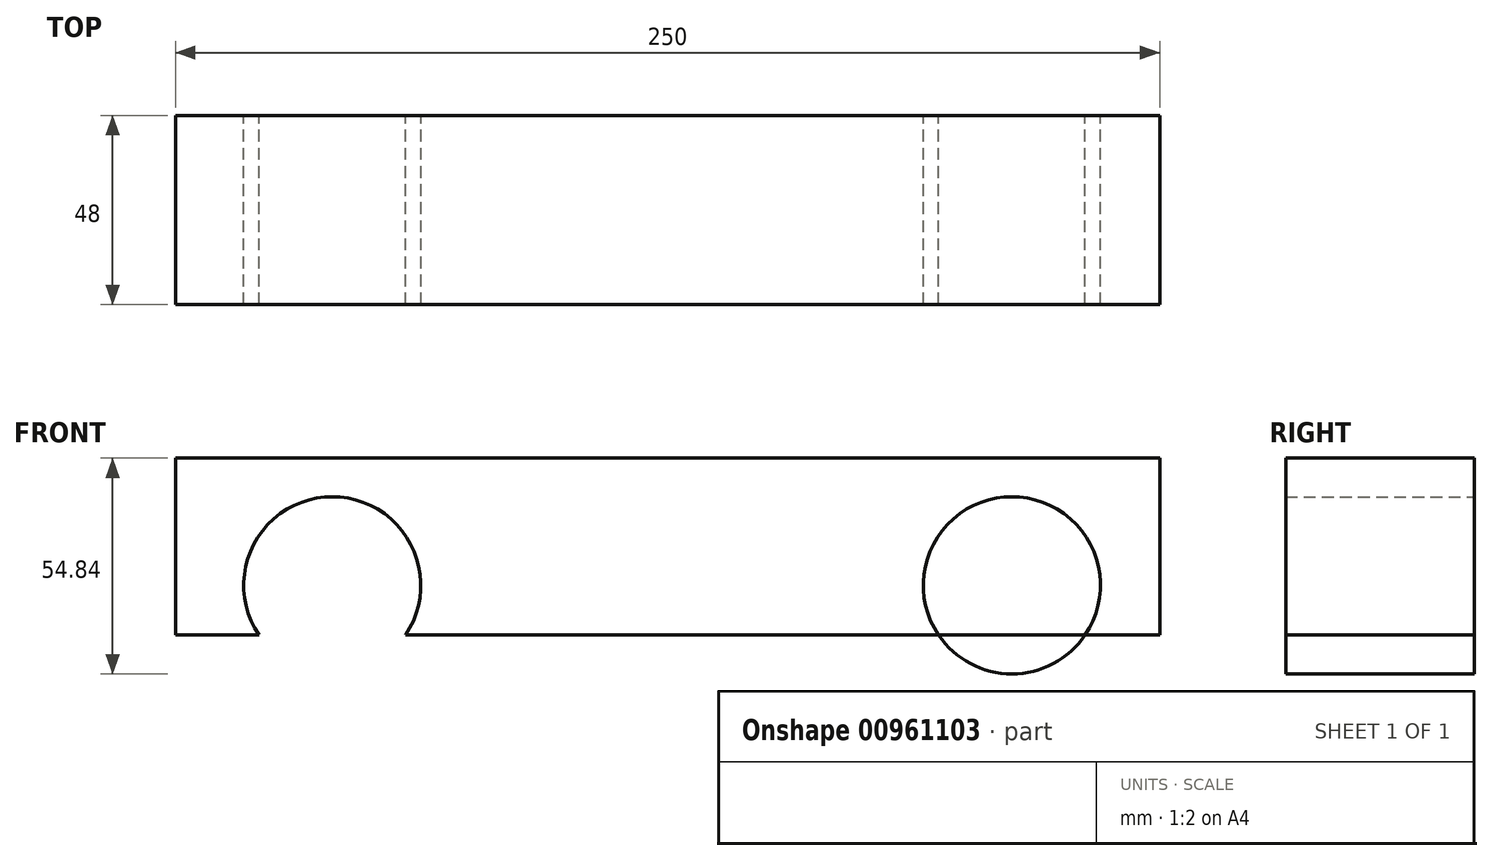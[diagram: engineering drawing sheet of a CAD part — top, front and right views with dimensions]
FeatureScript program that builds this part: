
annotation { "Feature Type Name" : "Feature", "Feature Type Description" : "" }
export const myFeature = defineFeature(function(context is Context, id is Id, definition is map)
    precondition{}
    {
        {
            var Q0;
            Q0=qCreatedBy(makeId("Front.planeOp"),FACE);
            var sketch = newSketch(context, id + "F0", { "sketchPlane" : qUnion([Q0])});
            skLineSegment(sketch, "E0.bottom", {"start": v(-111.8, 45) * mm, "end": v(138.2, 45) * mm});
            skLineSegment(sketch, "E0.top", {"start": v(-111.8, 0) * mm, "end": v(138.2, 0) * mm});
            skLineSegment(sketch, "E0.left", {"start": v(-111.8, 45) * mm, "end": v(-111.8, 0) * mm});
            skLineSegment(sketch, "E0.right", {"start": v(138.2, 45) * mm, "end": v(138.2, 0) * mm});
            skLineSegment(sketch, "E1.bottom", {"start": v(-74.7, 45) * mm, "end": v(75.05, 45) * mm});
            skLineSegment(sketch, "E1.top", {"start": v(-74.7, 89.93) * mm, "end": v(75.05, 89.93) * mm});
            skLineSegment(sketch, "E1.left", {"start": v(-74.7, 45) * mm, "end": v(-74.7, 89.93) * mm});
            skLineSegment(sketch, "E1.right", {"start": v(75.05, 45) * mm, "end": v(75.05, 89.93) * mm});
            skCircle(sketch, "E2", {"center": v(100.63, 12.66) * mm, "radius": 22.5 * mm});
            skCircle(sketch, "E3", {"center": v(-72.02, 12.66) * mm, "radius": 22.5 * mm});
            skSolve(sketch);
        }
        {
            var Q0;
            Q0=makeQuery(id+"F0.imprint","IMPRINT",FACE,{"disambiguationData":[TD([[makeQuery(id+"F0.imprint","IMPRINT",EDGE,{"derivedFrom":sQuery(id+"F0.wireOp",EDGE,"E1.bottom")}),1.0]])]});
            var Q1;
            {var subQ0=sQuery(id+"F0.wireOp",EDGE,"E3");var subQ1=sQuery(id+"F0.wireOp",EDGE,"E0.top");var subQ2=makeQuery(id+"F0.imprint","INTERSECT",VERTEX,{"disambiguationData":[OD(0.0)],"derivedFrom":[subQ1,subQ0]});Q1=makeQuery(id+"F0.imprint","IMPRINT",FACE,{"disambiguationData":[TD([[makeQuery(id+"F0.imprint","IMPRINT",EDGE,{"disambiguationData":[TD([[subQ2,-1.0]])],"derivedFrom":subQ1}),1.0]])]});}
            var Q2;
            {var subQ0=sQuery(id+"F0.wireOp",EDGE,"E3");var subQ1=sQuery(id+"F0.wireOp",EDGE,"E0.top");var subQ2=makeQuery(id+"F0.imprint","INTERSECT",VERTEX,{"disambiguationData":[OD(0.0)],"derivedFrom":[subQ1,subQ0]});Q2=makeQuery(id+"F0.imprint","IMPRINT",FACE,{"disambiguationData":[TD([[makeQuery(id+"F0.imprint","IMPRINT",EDGE,{"disambiguationData":[TD([[subQ2,-1.0]])],"derivedFrom":subQ1}),-1.0]])]});}
            var Q3;
            {var subQ5=sQuery(id+"F0.wireOp",EDGE,"E0.left");Q3=makeQuery(id+"F0.imprint","IMPRINT",FACE,{"disambiguationData":[TD([[makeQuery(id+"F0.imprint","IMPRINT",EDGE,{"derivedFrom":subQ5}),1.0]])]});}
            var Q4;
            {var subQ0=sQuery(id+"F0.wireOp",EDGE,"E2");var subQ1=sQuery(id+"F0.wireOp",EDGE,"E0.top");var subQ2=makeQuery(id+"F0.imprint","INTERSECT",VERTEX,{"disambiguationData":[OD(0.0)],"derivedFrom":[subQ1,subQ0]});Q4=makeQuery(id+"F0.imprint","IMPRINT",FACE,{"disambiguationData":[TD([[makeQuery(id+"F0.imprint","IMPRINT",EDGE,{"disambiguationData":[TD([[subQ2,-1.0]])],"derivedFrom":subQ1}),-1.0]])]});}
            extrude(context, id + "F1", {"entities" : qUnion([Q0, Q1, Q2, Q3, Q4]), "depth" : 48 * mm, "offsetDistance" : 25 * mm});
        }
    });
